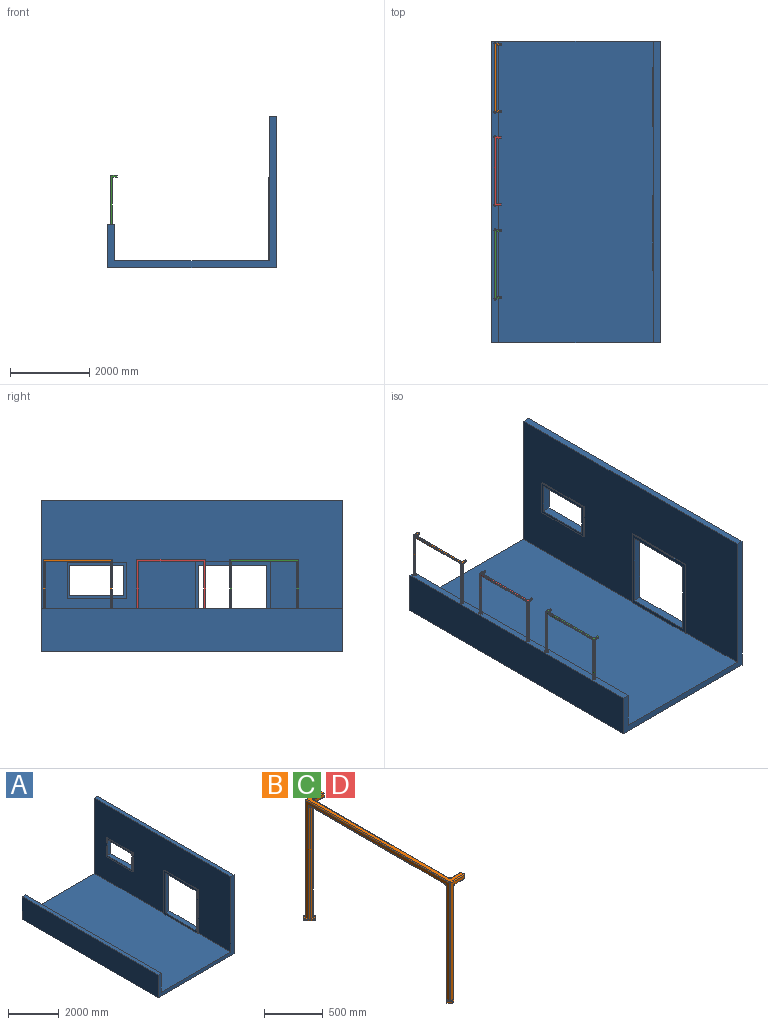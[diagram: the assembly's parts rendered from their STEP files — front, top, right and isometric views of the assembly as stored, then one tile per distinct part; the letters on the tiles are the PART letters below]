
ASSEMBLY  parts=4 mates=1
PART A: 27 faces, bbox 4254.5x7620x3835.4 mm
  f0: plane 7620x3835.4mm, normal (1,0,0), area 24846960.2mm2, adj f6,f7,f10,f11,f19,f20,f21,f22
  f1: plane 1498.6x914.4mm, normal (-1,0,0), area 313245.8mm2, adj f12,f13,f14,f15,f23,f24,f25,f26
  f2: plane 2114.55x1892.3mm, normal (-1,0,0), area 679649.2mm2, adj f8,f16,f17,f18,f19,f20,f21,f22
  f3: plane 7620x3657.6mm, normal (-1,0,0), area 22499229.2mm2, adj f7,f8,f10,f11,f12,f13,f14,f15
  f4: plane 7620x177.8mm, normal (0,0,1), area 1354836mm2, adj f5,f9,f10,f11
  f5: plane 7620x1092.2mm, normal (-1,0,0), area 8322564mm2, adj f4,f6,f10,f11
  f6: plane 7620x4254.5mm, normal (0,0,-1), area 32419290mm2, adj f0,f5,f10,f11
  f7: plane 7620x177.8mm, normal (0,0,1), area 1354836mm2, adj f0,f3,f10,f11
  f8: plane 7620x3898.9mm, normal (0,0,1), area 29661553.6mm2, adj f2,f3,f9,f10,f11,f16,f17
  f9: plane 7620x914.4mm, normal (1,0,0), area 6967728mm2, adj f4,f8,f10,f11
  f10: plane 4254.5x3835.4mm, normal (0,-1,0), area 1569351.7mm2, adj f0,f3,f4,f5,f6,f7,f8,f9
  f11: plane 4254.5x3835.4mm, normal (0,1,0), area 1569351.7mm2, adj f0,f3,f4,f5,f6,f7,f8,f9
  f12: plane 1498.6x25.4mm, normal (0,0,1), area 38064.4mm2, adj f1,f3,f13,f15
  f13: plane 914.4x25.4mm, normal (0,1,0), area 23225.8mm2, adj f1,f3,f12,f14
  f14: plane 1498.6x25.4mm, normal (0,0,-1), area 38064.4mm2, adj f1,f3,f13,f15
  f15: plane 914.4x25.4mm, normal (0,-1,0), area 23225.8mm2, adj f1,f3,f12,f14
  f16: plane 2114.55x25.4mm, normal (0,1,0), area 53709.6mm2, adj f2,f3,f8,f18
  f17: plane 2114.55x25.4mm, normal (0,-1,0), area 53709.6mm2, adj f2,f3,f8,f18
  f18: plane 1892.3x25.4mm, normal (0,0,1), area 48064.4mm2, adj f2,f3,f16,f17
  f19: plane 1731.27x203.2mm, normal (0,0,-1), area 351794.3mm2, adj f0,f2,f20,f22
  f20: plane 1918.66x203.2mm, normal (0,-1,0), area 389870.9mm2, adj f0,f2,f19,f21
  f21: plane 1731.27x203.2mm, normal (0,0,1), area 351794.3mm2, adj f0,f2,f20,f22
  f22: plane 1918.66x203.2mm, normal (0,1,0), area 389870.9mm2, adj f0,f2,f19,f21
  f23: plane 1368.82x203.2mm, normal (0,0,-1), area 278144.1mm2, adj f0,f1,f24,f26
  f24: plane 772.25x203.2mm, normal (0,-1,0), area 156921.7mm2, adj f0,f1,f23,f25
  f25: plane 1368.82x203.2mm, normal (0,0,1), area 278144.1mm2, adj f0,f1,f24,f26
  f26: plane 772.25x203.2mm, normal (0,1,0), area 156921.7mm2, adj f0,f1,f23,f25
PART B: 92 faces, bbox 208.1x1806.9x1244.6 mm
  f0: plane 1727.2x1222.38mm, normal (-1,0,0), area 130599mm2, adj f5,f9,f12,f24,f28,f31,f38,f57
  f1: plane 1222.38x168.28mm, normal (0,-1,0), area 43223mm2, adj f5,f20,f25,f26,f29,f55,f79
  f2: plane 1171.58x31.75mm, normal (0,1,0), area 37197.5mm2, adj f4,f24,f32,f83
  f3: plane 1171.58x31.75mm, normal (1,0,0), area 37197.5mm2, adj f4,f25,f33,f83
  f4: cylinder r=9.53mm len=1177.15mm, axis (0,0,-1), area 17557.3mm2, adj f2,f3,f47,f48,f83
  f5: cylinder r=9.53mm len=1222.38mm, axis (0,0,-1), area 18289mm2, adj f0,f1,f56,f79
  f6: plane 1171.58x31.75mm, normal (1,0,0), area 37197.5mm2, adj f10,f11,f44,f67
  f7: plane 1171.58x31.75mm, normal (0,-1,0), area 37197.5mm2, adj f9,f10,f40,f67
  f8: plane 1222.38x168.28mm, normal (0,1,0), area 43223mm2, adj f11,f12,f23,f45,f46,f59,f63
  f9: cylinder r=9.53mm len=1184.28mm, axis (0,0,-1), area 17581.7mm2, adj f0,f7,f16,f38,f63,f65,f66,f67
  f10: cylinder r=9.53mm len=1177.15mm, axis (0,0,1), area 17557.3mm2, adj f6,f7,f51,f52,f67
  f11: cylinder r=9.53mm len=1184.28mm, axis (0,0,-1), area 17581.7mm2, adj f6,f8,f16,f45,f63,f64,f67,f68
  f12: cylinder r=9.53mm len=1222.38mm, axis (0,0,1), area 18289mm2, adj f0,f8,f58,f63
  f13: plane 1625.6x31.75mm, normal (1,0,0), area 51612.8mm2, adj f35,f36,f41,f42
  f14: plane 111.48x111.48mm, normal (0,0,-1), area 5911.5mm2, adj f24,f25,f76,f77,f78,f80,f81,f82
  f15: plane 1625.6x31.75mm, normal (0,0,-1), area 51612.8mm2, adj f31,f32,f40,f41
  f16: plane 111.48x111.48mm, normal (0,0,-1), area 5911.5mm2, adj f9,f11,f60,f61,f62,f64,f65,f66
  f17: plane 1727.2x168.28mm, normal (0,0,1), area 63663.7mm2, adj f20,f23,f27,f30,f36,f37,f39,f55
  f18: plane 117.48x31.75mm, normal (0,0,-1), area 3729.8mm2, adj f20,f26,f33,f34
  f19: plane 117.48x31.75mm, normal (0,1,0), area 3729.8mm2, adj f20,f27,f34,f35
  f20: plane 50.8x50.8mm, normal (1,0,0), area 2502.8mm2, adj f1,f17,f18,f19,f26,f27,f34,f55
  f21: plane 117.48x31.75mm, normal (0,0,-1), area 3729.8mm2, adj f23,f43,f44,f46
  f22: plane 117.48x31.75mm, normal (0,-1,0), area 3729.8mm2, adj f23,f37,f42,f43
  f23: plane 50.8x50.8mm, normal (1,0,0), area 2502.8mm2, adj f8,f17,f21,f22,f37,f43,f46,f59
  f24: cylinder r=9.53mm len=1184.28mm, axis (0,0,1), area 17581.7mm2, adj f0,f2,f14,f28,f79,f81,f83,f84
  f25: cylinder r=9.53mm len=1184.28mm, axis (0,0,1), area 17581.7mm2, adj f1,f3,f14,f29,f79,f80,f82,f83
  f26: cylinder r=9.53mm len=117.48mm, axis (1,0,0), area 1757.6mm2, adj f1,f18,f20,f29
  f27: cylinder r=9.53mm len=117.48mm, axis (1,0,0), area 1757.6mm2, adj f17,f19,f20,f30
  f28: torus R=19.05mm, axis (1,0,0), area 305.2mm2, adj f0,f24,f31,f32
  f29: torus R=19.05mm, axis (0,-1,0), area 305.2mm2, adj f1,f25,f26,f33
  f30: torus R=19.05mm, axis (0,0,-1), area 305.2mm2, adj f17,f27,f35,f36
  f31: cylinder r=9.53mm len=1625.6mm, axis (0,1,0), area 24322mm2, adj f0,f15,f28,f38
  f32: cylinder r=9.53mm len=31.75mm, axis (1,0,0), area 475mm2, adj f2,f15,f28,f47
  f33: cylinder r=9.53mm len=31.75mm, axis (0,1,0), area 475mm2, adj f3,f18,f29,f48
  f34: cylinder r=9.53mm len=123.05mm, axis (1,0,0), area 1786.1mm2, adj f18,f19,f20,f48,f50
  f35: cylinder r=9.53mm len=31.75mm, axis (0,0,1), area 475mm2, adj f13,f19,f30,f50
  f36: cylinder r=9.53mm len=1625.6mm, axis (0,1,0), area 24322mm2, adj f13,f17,f30,f39
  f37: cylinder r=9.53mm len=117.48mm, axis (-1,0,0), area 1757.6mm2, adj f17,f22,f23,f39
  f38: torus R=19.05mm, axis (1,0,0), area 305.2mm2, adj f0,f9,f31,f40
  f39: torus R=19.05mm, axis (0,0,-1), area 305.2mm2, adj f17,f36,f37,f42
  f40: cylinder r=9.53mm len=31.75mm, axis (-1,0,0), area 475mm2, adj f7,f15,f38,f52
  f41: cylinder r=9.53mm len=1636.76mm, axis (0,-1,0), area 24378.8mm2, adj f13,f15,f47,f50,f52,f54
  f42: cylinder r=9.53mm len=31.75mm, axis (0,0,-1), area 475mm2, adj f13,f22,f39,f54
  f43: cylinder r=9.53mm len=123.05mm, axis (1,0,0), area 1786.1mm2, adj f21,f22,f23,f51,f54
  f44: cylinder r=9.53mm len=31.75mm, axis (0,1,0), area 475mm2, adj f6,f21,f45,f51
  f45: torus R=19.05mm, axis (0,-1,0), area 305.2mm2, adj f8,f11,f44,f46
  f46: cylinder r=9.53mm len=117.48mm, axis (1,0,0), area 1757.6mm2, adj f8,f21,f23,f45
  f47: bspline ~13.25x13.25mm, area 100.9mm2, adj f4,f32,f41,f49
  f48: bspline ~13.25x13.25mm, area 100.9mm2, adj f4,f33,f34,f49
  f49: sphere r=9.53mm, area 50mm2, adj f47,f48,f50
  f50: bspline ~13.25x13.25mm, area 100.9mm2, adj f34,f35,f41,f49
  f51: bspline ~13.25x13.25mm, area 100.9mm2, adj f10,f43,f44,f53
  f52: bspline ~13.25x13.25mm, area 100.9mm2, adj f10,f40,f41,f53
  f53: sphere r=9.53mm, area 50mm2, adj f51,f52,f54
  f54: bspline ~13.25x13.25mm, area 100.9mm2, adj f41,f42,f43,f53
  f55: cylinder r=9.53mm len=168.28mm, axis (1,0,0), area 2517.7mm2, adj f1,f17,f20,f56
  f56: sphere r=9.53mm, area 142.5mm2, adj f5,f55,f57
  f57: cylinder r=9.53mm len=1727.2mm, axis (0,-1,0), area 25842.1mm2, adj f0,f17,f56,f58
  f58: sphere r=9.53mm, area 142.5mm2, adj f12,f57,f59
  f59: cylinder r=9.53mm len=168.28mm, axis (-1,0,0), area 2517.7mm2, adj f8,f17,f23,f58
  f60: cylinder r=6.35mm len=12.7mm, axis (0,0,-1), area 126.7mm2, adj f16,f61,f63,f64
  f61: plane 35.92x35.92mm, normal (-0.71,0.71,0), area 645.2mm2, adj f16,f60,f62,f63
  f62: cylinder r=6.35mm len=12.7mm, axis (0,0,-1), area 126.7mm2, adj f16,f61,f63,f65
  f63: plane 76.73x76.73mm, normal (0,0,1), area 1704.4mm2, adj f0,f8,f9,f11,f12,f60,f61,f62
  f64: plane 29.97x29.97mm, normal (0.71,0.71,0), area 538.3mm2, adj f11,f16,f60,f63
  f65: plane 29.97x29.97mm, normal (-0.71,-0.71,0), area 538.3mm2, adj f9,f16,f62,f63
  f66: plane 29.97x29.97mm, normal (-0.71,-0.71,0), area 538.3mm2, adj f9,f16,f67,f71
  f67: plane 76.73x76.73mm, normal (0,0,1), area 1704.4mm2, adj f6,f7,f9,f10,f11,f66,f68,f69
  f68: plane 29.97x29.97mm, normal (0.71,0.71,0), area 538.3mm2, adj f11,f16,f67,f69
  f69: cylinder r=6.35mm len=12.7mm, axis (0,0,-1), area 126.7mm2, adj f16,f67,f68,f70
  f70: plane 35.92x35.92mm, normal (0.71,-0.71,0), area 645.2mm2, adj f16,f67,f69,f71
  f71: cylinder r=6.35mm len=12.7mm, axis (0,0,-1), area 126.7mm2, adj f16,f66,f67,f70
  f72: cylinder r=6.35mm len=12.7mm, axis (0,0,-1), area 506.7mm2, adj f16,f67
  f73: cylinder r=6.35mm len=12.7mm, axis (0,0,-1), area 506.7mm2, adj f16,f67
  f74: cylinder r=6.35mm len=12.7mm, axis (0,0,-1), area 506.7mm2, adj f16,f63
  f75: cylinder r=6.35mm len=12.7mm, axis (0,0,-1), area 506.7mm2, adj f16,f63
  f76: cylinder r=6.35mm len=12.7mm, axis (0,0,-1), area 126.7mm2, adj f14,f77,f79,f81
  f77: plane 35.92x35.92mm, normal (-0.71,-0.71,0), area 645.2mm2, adj f14,f76,f78,f79
  f78: cylinder r=6.35mm len=12.7mm, axis (0,0,-1), area 126.7mm2, adj f14,f77,f79,f80
  f79: plane 76.73x76.73mm, normal (0,0,1), area 1704.4mm2, adj f0,f1,f5,f24,f25,f76,f77,f78
  f80: plane 29.97x29.97mm, normal (0.71,-0.71,0), area 538.3mm2, adj f14,f25,f78,f79
  f81: plane 29.97x29.97mm, normal (-0.71,0.71,0), area 538.3mm2, adj f14,f24,f76,f79
  f82: plane 29.97x29.97mm, normal (0.71,-0.71,0), area 538.3mm2, adj f14,f25,f83,f87
  f83: plane 76.73x76.73mm, normal (0,0,1), area 1704.4mm2, adj f2,f3,f4,f24,f25,f82,f84,f85
  f84: plane 29.97x29.97mm, normal (-0.71,0.71,0), area 538.3mm2, adj f14,f24,f83,f85
  f85: cylinder r=6.35mm len=12.7mm, axis (0,0,-1), area 126.7mm2, adj f14,f83,f84,f86
  f86: plane 35.92x35.92mm, normal (0.71,0.71,0), area 645.2mm2, adj f14,f83,f85,f87
  f87: cylinder r=6.35mm len=12.7mm, axis (0,0,-1), area 126.7mm2, adj f14,f82,f83,f86
  f88: cylinder r=6.35mm len=12.7mm, axis (0,0,-1), area 506.7mm2, adj f14,f83
  f89: cylinder r=6.35mm len=12.7mm, axis (0,0,-1), area 506.7mm2, adj f14,f83
  f90: cylinder r=6.35mm len=12.7mm, axis (0,0,-1), area 506.7mm2, adj f14,f79
  f91: cylinder r=6.35mm len=12.7mm, axis (0,0,-1), area 506.7mm2, adj f14,f79
PART C: same geometry as B
PART D: same geometry as B
PLACE A at identity fixed
PLACE B t=(-114.75,-917.83,914.4)mm
PLACE C t=(-114.75,-5642.23,914.4)mm
PLACE D t=(-114.75,-3280.03,914.4)mm
MATE planar A.f4 <-> B.f16  axis (0,0,1) through (-88.9,-3810,914.4)mm
